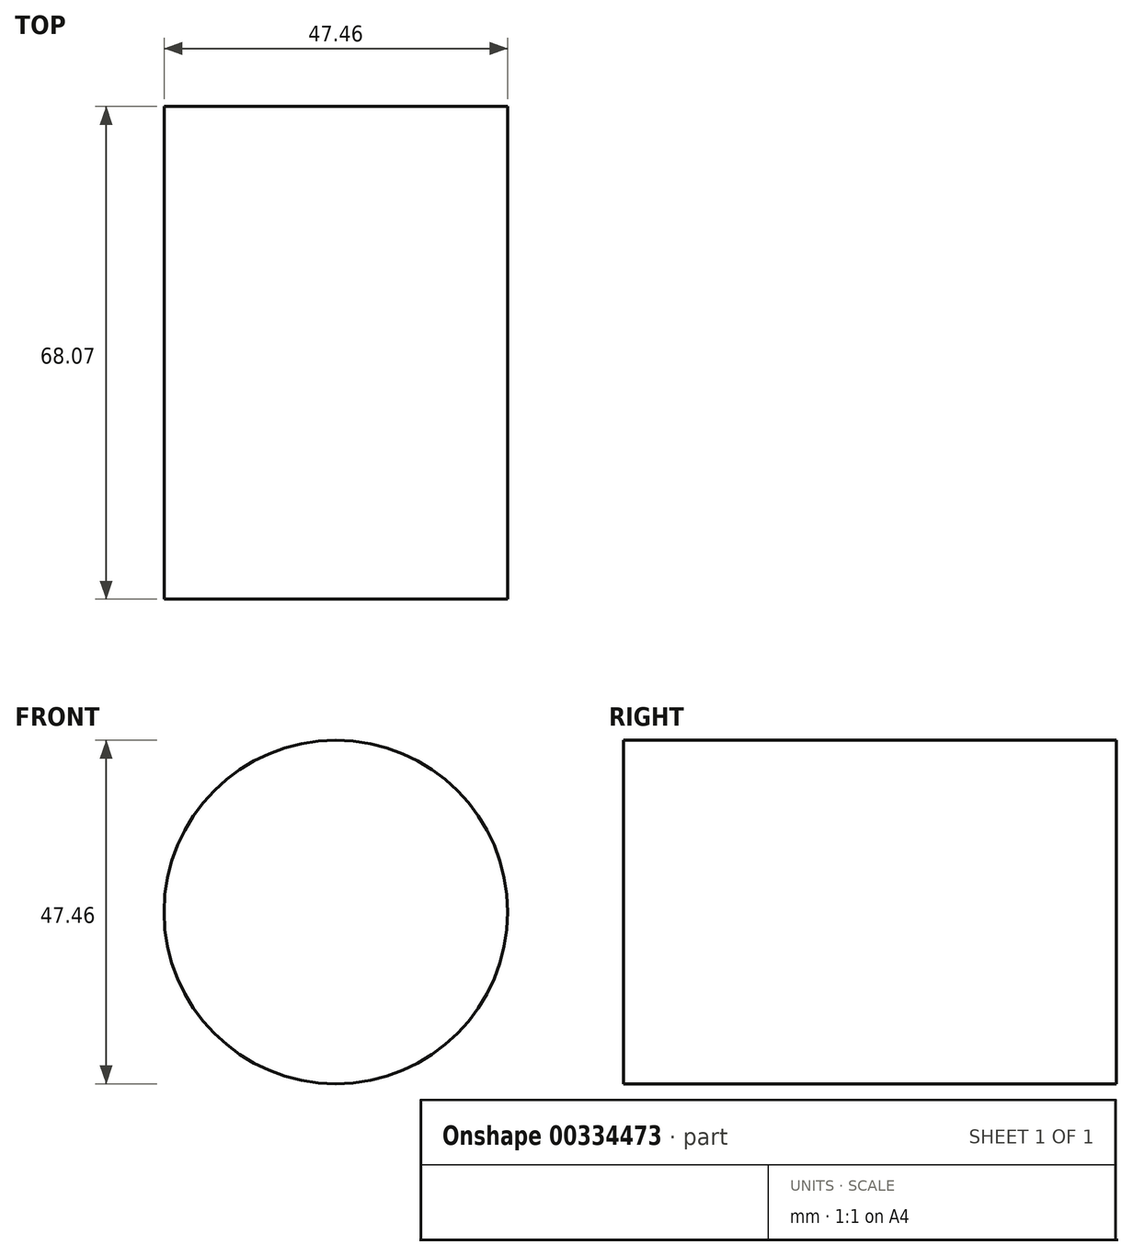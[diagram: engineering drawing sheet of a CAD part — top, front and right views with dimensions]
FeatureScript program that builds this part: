
annotation { "Feature Type Name" : "Feature", "Feature Type Description" : "" }
export const myFeature = defineFeature(function(context is Context, id is Id, definition is map)
    precondition{}
    {
        {
            var Q0;
            Q0=qCreatedBy(makeId("Front.planeOp"),FACE);
            var sketch = newSketch(context, id + "F0", { "sketchPlane" : qUnion([Q0])});
            skCircle(sketch, "E0", {"center": v(-92.95, 5.28) * mm, "radius": 23.73 * mm});
            skSolve(sketch);
        }
        {
            var Q0;
            Q0 = qSketchRegion(id + "F0", true);
            extrude(context, id + "F1", {"entities" : qUnion([Q0]), "oppositeDirection" : true, "depth" : 68.07 * mm});
        }
    });
